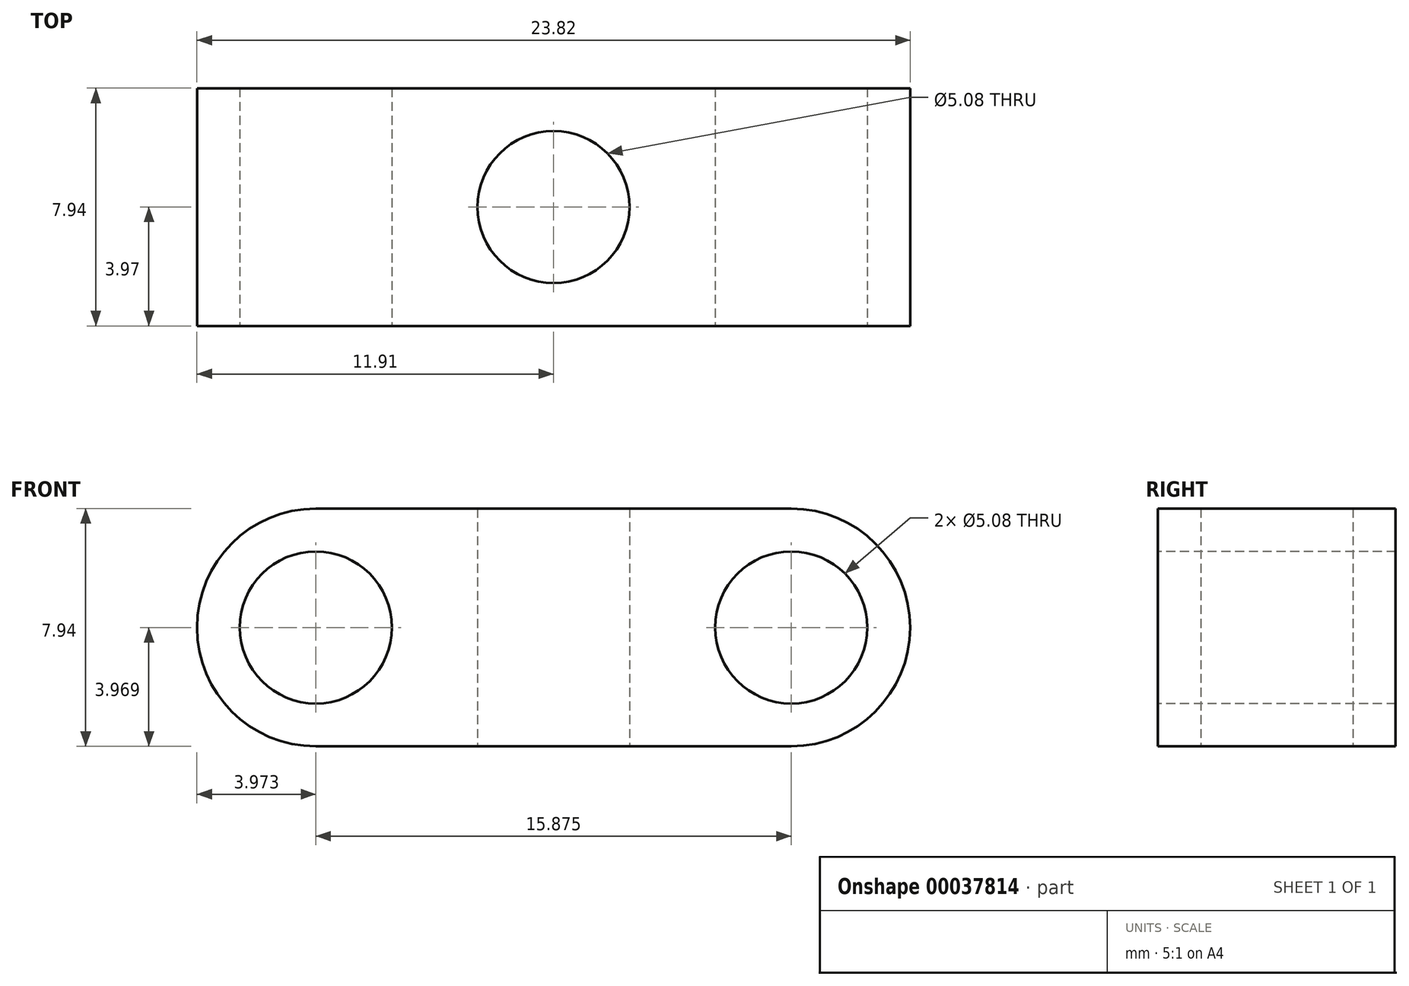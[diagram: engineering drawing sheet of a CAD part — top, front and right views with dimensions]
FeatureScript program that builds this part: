
annotation { "Feature Type Name" : "Feature", "Feature Type Description" : "" }
export const myFeature = defineFeature(function(context is Context, id is Id, definition is map)
    precondition{}
    {
        {
            var Q0;
            Q0=qCreatedBy(makeId("Top.planeOp"),FACE);
            var sketch = newSketch(context, id + "F0", { "sketchPlane" : qUnion([Q0])});
            skLineSegment(sketch, "E0.rect.bottom", {"start": v(11.9, -3.97) * mm, "end": v(-11.9, -3.97) * mm});
            skLineSegment(sketch, "E0.rect.top", {"start": v(11.9, 3.97) * mm, "end": v(-11.9, 3.97) * mm});
            skLineSegment(sketch, "E0.rect.left", {"start": v(11.9, -3.97) * mm, "end": v(11.9, 3.97) * mm});
            skLineSegment(sketch, "E0.rect.right", {"start": v(-11.9, -3.97) * mm, "end": v(-11.9, 3.97) * mm});
            skPoint(sketch, "E0.rect.middle", {"position": v(0, 0) * mm});
            skCircle(sketch, "E1", {"center": v(0, 0) * mm, "radius": 2.54 * mm});
            skSolve(sketch);
        }
        {
            var Q0;
            Q0 = qSketchRegion(id + "F0", true);
            extrude(context, id + "F1", {"entities" : qUnion([Q0]), "depth" : 7.94 * mm});
        }
        {
            var Q0;
            Q0=makeQuery(id+"F1.opExtrude","SWEPT_FACE",FACE,{"disambiguationData":[OSD([sQuery(id+"F0.wireOp",EDGE,"E0.rect.bottom")])]});
            var sketch = newSketch(context, id + "F2", { "sketchPlane" : qUnion([Q0])});
            skLineSegment(sketch, "E2", {"start": v(-11.9, 3.97) * mm, "end": v(-7.94, 3.97) * mm});
            skLineSegment(sketch, "E3", {"start": v(-7.94, 3.97) * mm, "end": v(7.94, 3.97) * mm});
            skLineSegment(sketch, "E4", {"start": v(7.94, 3.97) * mm, "end": v(11.9, 3.97) * mm});
            skCircle(sketch, "E5", {"center": v(-7.94, 3.97) * mm, "radius": 2.54 * mm});
            skCircle(sketch, "E6", {"center": v(7.94, 3.97) * mm, "radius": 2.54 * mm});
            skSolve(sketch);
        }
        {
            var Q0;
            Q0 = qSketchRegion(id + "F2", true);
            var Q1;
            Q1=makeQuery(id+"F1.opExtrude","SWEPT_FACE",FACE,{"disambiguationData":[OSD([sQuery(id+"F0.wireOp",EDGE,"E0.rect.top")])]});
            extrude(context, id + "F3", {"entities" : qUnion([Q0]), "operationType" : NewBodyOperationType.REMOVE, "endBound" : BoundingType.UP_TO_SURFACE, "oppositeDirection" : true, "endBoundEntityFace" : qUnion([Q1]), "depth" : 25.4 * mm});
        }
        {
            var Q0;
            Q0=makeQuery(id+"F1.opExtrude","CAP_EDGE",EDGE,{"disambiguationData":[OSD([sQuery(id+"F0.wireOp",EDGE,"E0.rect.left")])],"isStart":false});
            var Q1;
            Q1=makeQuery(id+"F1.opExtrude","CAP_EDGE",EDGE,{"disambiguationData":[OSD([sQuery(id+"F0.wireOp",EDGE,"E0.rect.left")])],"isStart":true});
            var Q2;
            Q2=makeQuery(id+"F1.opExtrude","CAP_EDGE",EDGE,{"disambiguationData":[OSD([sQuery(id+"F0.wireOp",EDGE,"E0.rect.right")])],"isStart":false});
            var Q3;
            Q3=makeQuery(id+"F1.opExtrude","CAP_EDGE",EDGE,{"disambiguationData":[OSD([sQuery(id+"F0.wireOp",EDGE,"E0.rect.right")])],"isStart":true});
            fillet(context, id + "F4", {"entities" : qUnion([Q0, Q1, Q2, Q3]), "radius" : 3.97 * mm, "tangentPropagation" : true, "allowEdgeOverflow" : false});
        }
    });
